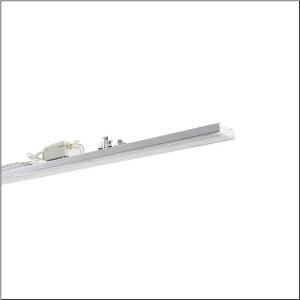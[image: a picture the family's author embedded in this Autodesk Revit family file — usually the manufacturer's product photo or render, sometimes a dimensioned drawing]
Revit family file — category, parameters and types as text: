
# Revit family: licross_r__11_recessed_mo_51tl14dv4exg_cd34
name_source: partatom
category: Lighting Fixtures
units: mm (PartAtom-declared; Revit-internal decimal feet)

## family parameters
Cut with Voids When Loaded = No
Host = Face
Light Source = No
Part Type = Normal
Room Calculation Point = No
Round Connector Dimension = Use Diameter
Shared = No

## types (1)
- --- (1 x LED, 14140 lm, 84.1 W, 4000K)
    Apparent Load = 84 VA
    CIE Flux Codes = 56 84 97 100 100
    Color Rendering = 80
    Color Temperature = 4000K
    Default Elevation = 1800 mm
    Description = Licross® 11 Recessed MO, luminaire insert, of sheet steel, coil coated, white, length: 2.250mm, width: 66mm, height: 67mm, LED rated luminous flux: 14.140lm, light colour: 840, control gear: DALI 2, with plug, 5-pole, with phase selection, mains connection: 220..240V, AC, 50/60Hz, rated input power: 84W, halogen-free wiring, primary light control with lens, of plastic, primary optical cover: cover, of PMMA, light emission: direct distribution, primary light characteristic: asymmetric, protection rating (complete): IP40, insulation class (complete): insulation class I (protective earthing), certification: CE, ENEC, VDE, UKCA, protection symbol: D if used in an environment without relevant dust loads with corresponding accessories, impact resistance: IK06, permissible ambient temperature for indoor applications: -25..+35°C, corresponds to IFS (International Featured Standards) requirements for safety and quality in the food industry, reducing of maximum allowable ambient temperature of 5°C with ceiling mounting, LABS conformity tested according to VDMA 24364:2018-05, packaging unit: 1 piece
    Height = 58 mm
    Lamp = 1 x LED
    Lamp Light Flux = 14140 lm
    Lamp Power = 84.1 W
    Lamp count = 1
    Length = 2250 mm
    Luminous efficacy = 168 lm/W
    Manufacturer = Siteco
    ModVariant = No
    Model = 51TL14DV4EXG
    Mounting Place = Ceiling
    Mounting Type = Pendant
    Number of Poles = 1
    OnlyDefault = Yes
    Power Factor = 1
    Product Name = Licross® 11 Recessed MO
    Product group = luminaire insert
    ProductGroupID = 901
    Protection Class = Protection class I
    Protection Degree = IP 40
    RLX_Detail_Level = 1
    RLX_Emergency_Light_Flux = 0 lm
    RLX_Emergency_Type = 0
    RLX_Emergency_Type_DB = No
    RlxData = <blob elided: 29997 chars, md5=60ee1fb2>
    Socket = socket
    Standby Power = 0 W
    System Light Flux = 14140 lm
    System Power = 84 W
    Type Comments = factory setting: luminous flux: 100 % | dim-lin: 254 | 378 mA
    Type Image = l_1296930.jpg
    URL = http://relux.com
    VarID = @adj_095294
    Voltage = 0 V
    Weight = 0.00 kg
    Width = 66 mm

## geometry (parser evidence)
native form markers: Blend x4, Sweep x10
no freeform markers — native parametric forms only
